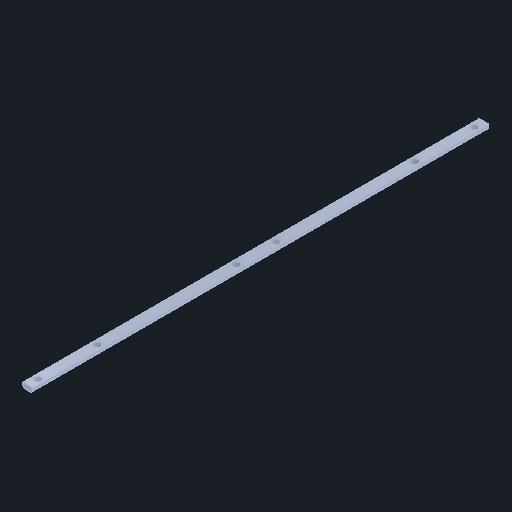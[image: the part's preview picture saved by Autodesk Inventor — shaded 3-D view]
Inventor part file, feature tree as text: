
AUTODESK INVENTOR PART (.ipt)
format: ipt  version: 2025 (Build 290162000, 162)  size: 189,440 bytes
history: native  units: in
note: dims shown in document units (in); Inventor stores cm internally (conversion verified against a paired STEP export)
features: extrude x4, sketch x4, thicken_offset x1, other x1
ambient origin geometry x8: Origin, YZ Plane, XZ Plane, XY Plane, X Axis, Y Axis, Z Axis, Center Point
bodies: Solid1 (feature_tree)
feature tree (10):
  extrude  "Extrusion1"  Depth=12.1875in
  thicken_offset  "Thicken1"
  extrude  "Extrusion2"  Depth=12.625in
  extrude  "Extrusion3"  Depth=0.165in
  extrude  "Extrusion4"  Depth=0.25in
  sketch  "Sketch2"  dims[d0=0.0625in d1=0.0in d2=12.1875in]
  sketch  "Sketch3"  dims[d3=12.125in d4=12.625in]
  sketch  "Sketch4"  dims[d5=0.0in d6=0.165in]
  sketch  "Sketch5"  dims[d7=0.165in d8=11.0in d9=0.25in d10=11.0in d11=0.0in d12=0.125in d13=0.0in d14=1.5in d15=0.165in d16=0.165in d17=0.165in d18=0.165in]
  other  "Cut-Revolve3"
